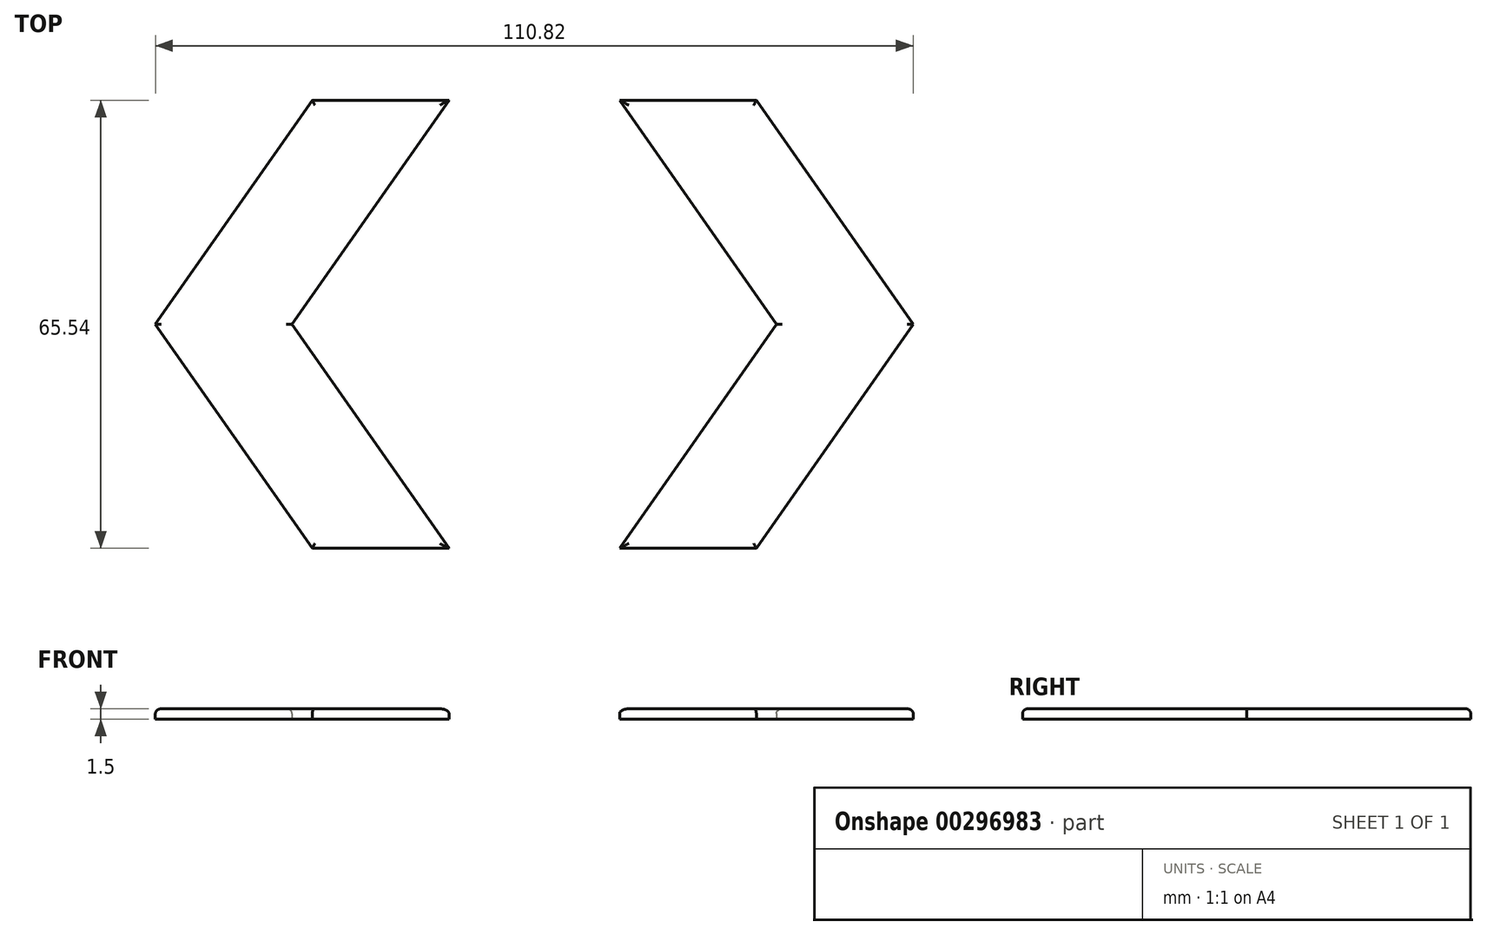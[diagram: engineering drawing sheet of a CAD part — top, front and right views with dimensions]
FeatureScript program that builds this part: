
annotation { "Feature Type Name" : "Feature", "Feature Type Description" : "" }
export const myFeature = defineFeature(function(context is Context, id is Id, definition is map)
    precondition{}
    {
        {
            var Q0;
            Q0=qCreatedBy(makeId("Top.planeOp"),FACE);
            var sketch = newSketch(context, id + "F0", { "sketchPlane" : qUnion([Q0])});
            skLineSegment(sketch, "E0", {"start": v(-55.41, 0) * mm, "end": v(-32.47, 32.77) * mm});
            skLineSegment(sketch, "E1", {"start": v(-35.41, 0) * mm, "end": v(-12.47, 32.77) * mm});
            skLineSegment(sketch, "E2", {"start": v(-12.47, 32.77) * mm, "end": v(-32.47, 32.77) * mm});
            skLineSegment(sketch, "E3", {"start": v(-55.41, 0) * mm, "end": v(-32.47, -32.77) * mm});
            skLineSegment(sketch, "E4", {"start": v(-35.41, 0) * mm, "end": v(-12.47, -32.77) * mm});
            skLineSegment(sketch, "E5", {"start": v(-12.47, -32.77) * mm, "end": v(-32.47, -32.77) * mm});
            skLineSegment(sketch, "E6.MirrorCS", {"start": v(12.47, 32.77) * mm, "end": v(32.47, 32.77) * mm});
            skLineSegment(sketch, "E7.MirrorCS", {"start": v(35.41, 0) * mm, "end": v(12.47, 32.77) * mm});
            skLineSegment(sketch, "E8.MirrorCS", {"start": v(12.47, -32.77) * mm, "end": v(32.47, -32.77) * mm});
            skLineSegment(sketch, "E9.MirrorCS", {"start": v(55.41, 0) * mm, "end": v(32.47, -32.77) * mm});
            skLineSegment(sketch, "E10.MirrorCS", {"start": v(55.41, 0) * mm, "end": v(32.47, 32.77) * mm});
            skLineSegment(sketch, "E11.MirrorCS", {"start": v(35.41, 0) * mm, "end": v(12.47, -32.77) * mm});
            skSolve(sketch);
        }
        {
            var Q0;
            Q0 = qSketchRegion(id + "F0", true);
            extrude(context, id + "F1", {"entities" : qUnion([Q0]), "depth" : 1.5 * mm, "offsetDistance" : 25 * mm});
        }
        {
            var Q0;
            Q0=makeQuery(id+"F1.opExtrude","CAP_FACE",FACE,{"disambiguationData":[OSD([sQuery(id+"F0.wireOp",EDGE,"E0"),sQuery(id+"F0.wireOp",EDGE,"E1"),sQuery(id+"F0.wireOp",EDGE,"E2"),sQuery(id+"F0.wireOp",EDGE,"E3"),sQuery(id+"F0.wireOp",EDGE,"E4"),sQuery(id+"F0.wireOp",EDGE,"E5")])],"isStart":false});
            var Q1;
            Q1=makeQuery(id+"F1.opExtrude","CAP_FACE",FACE,{"disambiguationData":[OSD([sQuery(id+"F0.wireOp",EDGE,"E6.MirrorCS"),sQuery(id+"F0.wireOp",EDGE,"E7.MirrorCS"),sQuery(id+"F0.wireOp",EDGE,"E8.MirrorCS"),sQuery(id+"F0.wireOp",EDGE,"E9.MirrorCS"),sQuery(id+"F0.wireOp",EDGE,"E10.MirrorCS"),sQuery(id+"F0.wireOp",EDGE,"E11.MirrorCS")])],"isStart":false});
            fillet(context, id + "F2", {"entities" : qUnion([Q0, Q1]), "radius" : .7 * mm, "tangentPropagation" : true, "allowEdgeOverflow" : false});
        }
    });
